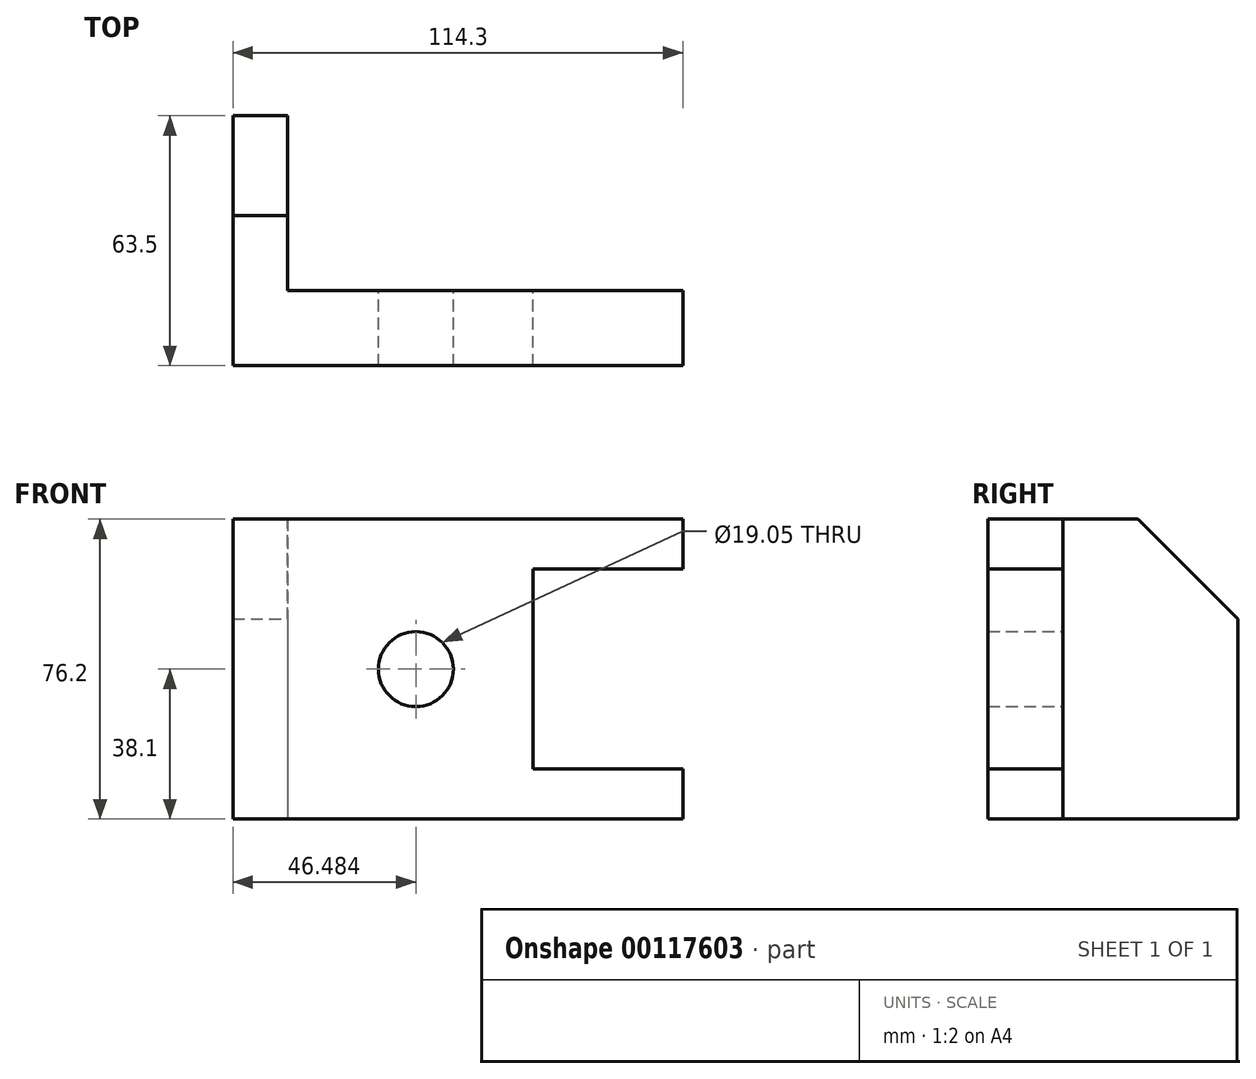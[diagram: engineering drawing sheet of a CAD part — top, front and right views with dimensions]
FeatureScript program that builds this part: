
annotation { "Feature Type Name" : "Feature", "Feature Type Description" : "" }
export const myFeature = defineFeature(function(context is Context, id is Id, definition is map)
    precondition{}
    {
        {
            var Q0;
            Q0=qCreatedBy(makeId("Top.planeOp"),FACE);
            var sketch = newSketch(context, id + "F0", { "sketchPlane" : qUnion([Q0])});
            skLineSegment(sketch, "E0", {"start": v(-84.39, 25.97) * mm, "end": v(-84.39, -37.53) * mm});
            skLineSegment(sketch, "E1", {"start": v(-84.39, -37.53) * mm, "end": v(29.91, -37.53) * mm});
            skLineSegment(sketch, "E2", {"start": v(29.91, -37.53) * mm, "end": v(29.91, -18.48) * mm});
            skLineSegment(sketch, "E3", {"start": v(29.91, -18.48) * mm, "end": v(-70.44, -18.48) * mm});
            skLineSegment(sketch, "E4", {"start": v(-70.44, -18.48) * mm, "end": v(-70.44, 25.97) * mm});
            skLineSegment(sketch, "E5", {"start": v(-70.44, 25.97) * mm, "end": v(-84.39, 25.97) * mm});
            skSolve(sketch);
        }
        {
            var Q0;
            Q0 = qSketchRegion(id + "F0", true);
            var Q1;
            Q1=makeQuery(id+"F0.imprint","IMPRINT",FACE,{"disambiguationData":[TD([[makeQuery(id+"F0.imprint","IMPRINT",EDGE,{"derivedFrom":sQuery(id+"F0.wireOp",EDGE,"E0")}),1.0]])]});
            extrude(context, id + "F1", {"entities" : qUnion([Q0, Q1]), "depth" : 76.2 * mm});
        }
        {
            var Q0;
            Q0=makeQuery(id+"F1.opExtrude","CAP_EDGE",EDGE,{"disambiguationData":[OSD([sQuery(id+"F0.wireOp",EDGE,"E5")])],"isStart":false});
            chamfer(context, id + "F2", {"entities" : qUnion([Q0]), "width" : 25.4 * mm, "tangentPropagation" : true});
        }
        {
            var Q0;
            Q0=makeQuery(id+"F1.opExtrude","SWEPT_FACE",FACE,{"disambiguationData":[OSD([sQuery(id+"F0.wireOp",EDGE,"E3")])]});
            var sketch = newSketch(context, id + "F3", { "sketchPlane" : qUnion([Q0])});
            skCircle(sketch, "E6", {"center": v(37.9, 38.1) * mm, "radius": 9.53 * mm});
            skSolve(sketch);
        }
        {
            var Q0;
            Q0=makeQuery(id+"F3.imprint","IMPRINT",FACE,{"disambiguationData":[TD([[makeQuery(id+"F3.imprint","IMPRINT",EDGE,{"derivedFrom":sQuery(id+"F3.wireOp",EDGE,"E6")}),1.0]])]});
            extrude(context, id + "F4", {"entities" : qUnion([Q0]), "operationType" : NewBodyOperationType.REMOVE, "endBound" : BoundingType.THROUGH_ALL, "oppositeDirection" : true, "depth" : 25.4 * mm});
        }
        {
            var Q0;
            Q0=makeQuery(id+"F1.opExtrude","SWEPT_FACE",FACE,{"disambiguationData":[OSD([sQuery(id+"F0.wireOp",EDGE,"E3")])]});
            var sketch = newSketch(context, id + "F5", { "sketchPlane" : qUnion([Q0])});
            skLineSegment(sketch, "E7", {"start": v(-29.91, 63.5) * mm, "end": v(8.19, 63.5) * mm});
            skLineSegment(sketch, "E8", {"start": v(8.19, 63.5) * mm, "end": v(8.19, 12.7) * mm});
            skLineSegment(sketch, "E9", {"start": v(8.19, 12.7) * mm, "end": v(-29.91, 12.7) * mm});
            skSolve(sketch);
        }
        {
            var Q0;
            Q0 = qSketchRegion(id + "F5", true);
            var Q1;
            {var subQ0=sQuery(id+"F5.wireOp",EDGE,"E7");Q1=makeQuery(id+"F5.imprint","IMPRINT",FACE,{"disambiguationData":[TD([[makeQuery(id+"F5.imprint","IMPRINT",EDGE,{"derivedFrom":subQ0}),-1.0]])]});}
            extrude(context, id + "F6", {"entities" : qUnion([Q0, Q1]), "operationType" : NewBodyOperationType.REMOVE, "endBound" : BoundingType.THROUGH_ALL, "oppositeDirection" : true, "depth" : 25.4 * mm});
        }
    });
